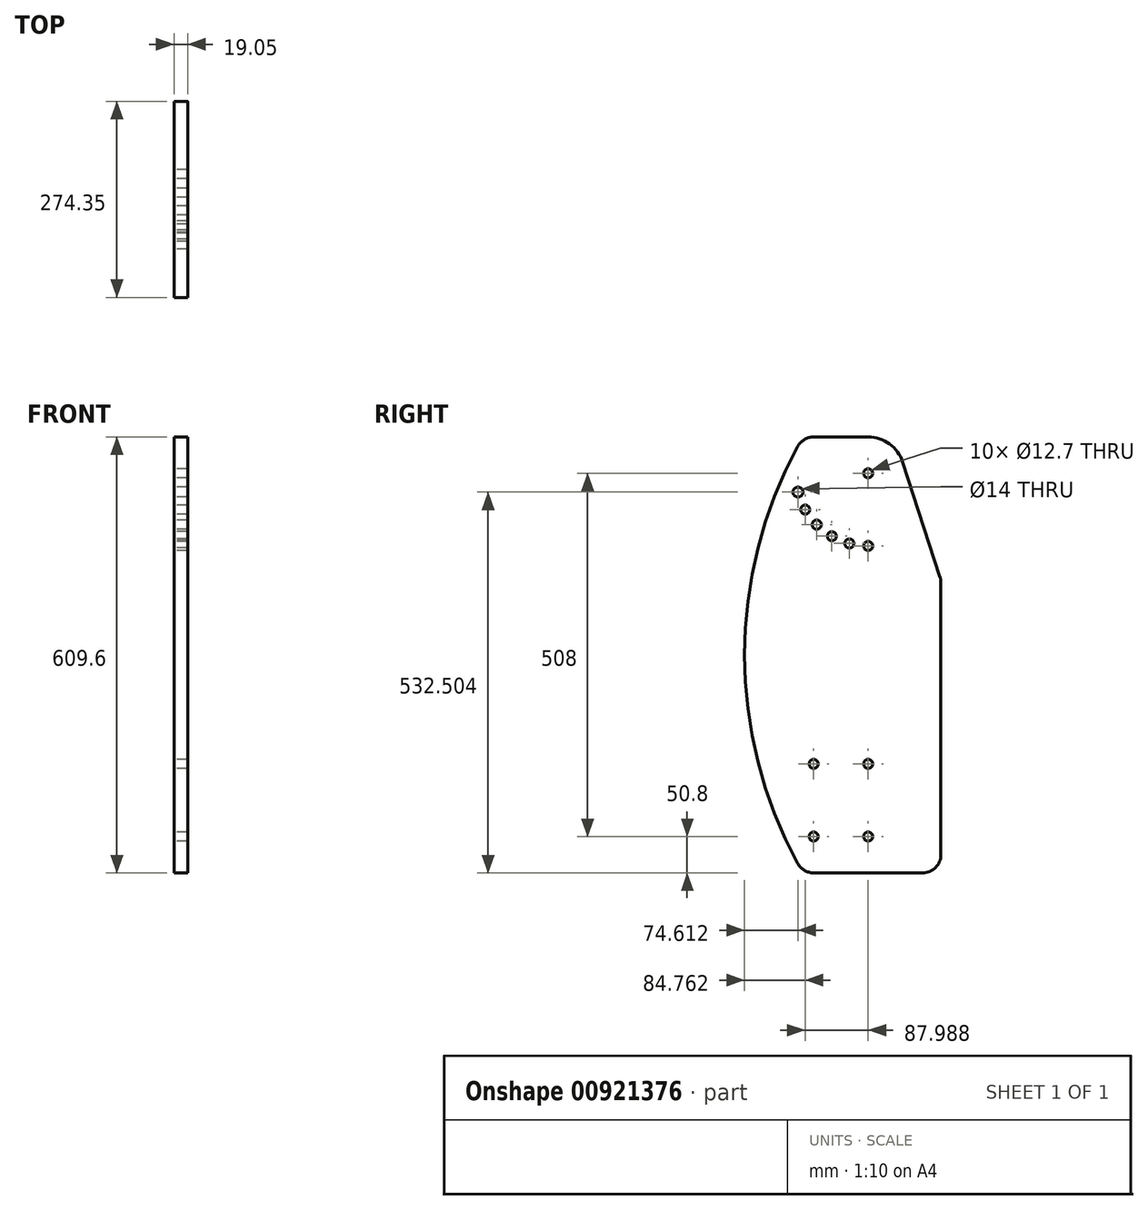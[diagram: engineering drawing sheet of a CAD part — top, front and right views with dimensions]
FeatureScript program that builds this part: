
annotation { "Feature Type Name" : "Feature", "Feature Type Description" : "" }
export const myFeature = defineFeature(function(context is Context, id is Id, definition is map)
    precondition{}
    {
        {
            var Q0;
            Q0=qCreatedBy(makeId("Right.planeOp"),FACE);
            var sketch = newSketch(context, id + "F0", { "sketchPlane" : qUnion([Q0])});
            skLineSegment(sketch, "E0.bottom", {"start": v(-101.6, 304.8) * mm, "end": v(101.6, 304.8) * mm, "construction": true});
            skLineSegment(sketch, "E0.top", {"start": v(-101.6, -304.8) * mm, "end": v(101.6, -304.8) * mm, "construction": true});
            skLineSegment(sketch, "E0.left", {"start": v(-101.6, 304.8) * mm, "end": v(-101.6, -304.8) * mm, "construction": true});
            skLineSegment(sketch, "E0.right", {"start": v(101.6, 304.8) * mm, "end": v(101.6, -304.8) * mm, "construction": true});
            skLineSegment(sketch, "E1", {"start": v(-101.6, 304.8) * mm, "end": v(101.6, -304.8) * mm, "construction": true});
            skLineSegment(sketch, "E2", {"start": v(0, 304.8) * mm, "end": v(0, -304.8) * mm, "construction": true});
            skCircle(sketch, "E3", {"center": v(0, 254) * mm, "radius": 6.35 * mm});
            skArc(sketch, "E4", {"start": v(101.6, 254) * mm, "mid": v(-74.05, 323.56) * mm, "end": v(6.35, 152.6) * mm, "construction": true});
            skCircle(sketch, "E5", {"center": v(0, 152.4) * mm, "radius": 6.35 * mm});
            skLineSegment(sketch, "E6", {"start": v(0, 254) * mm, "end": v(-26.3, 155.86) * mm});
            skLineSegment(sketch, "E7", {"start": v(0, 254) * mm, "end": v(-50.8, 166.01) * mm});
            skLineSegment(sketch, "E8", {"start": v(0, 254) * mm, "end": v(-71.84, 182.16) * mm});
            skLineSegment(sketch, "E9", {"start": v(0, 254) * mm, "end": v(-87.99, 203.2) * mm});
            skCircle(sketch, "E10", {"center": v(-26.3, 155.86) * mm, "radius": 6.35 * mm});
            skCircle(sketch, "E11", {"center": v(-50.8, 166.01) * mm, "radius": 6.35 * mm});
            skCircle(sketch, "E12", {"center": v(-71.84, 182.16) * mm, "radius": 6.35 * mm});
            skCircle(sketch, "E13", {"center": v(-87.99, 203.2) * mm, "radius": 6.35 * mm});
            skLineSegment(sketch, "E14.bottom", {"start": v(-76.2, -152.4) * mm, "end": v(0, -152.4) * mm, "construction": true});
            skLineSegment(sketch, "E14.top", {"start": v(-76.2, -254) * mm, "end": v(0, -254) * mm, "construction": true});
            skLineSegment(sketch, "E14.left", {"start": v(-76.2, -152.4) * mm, "end": v(-76.2, -254) * mm, "construction": true});
            skLineSegment(sketch, "E14.right", {"start": v(0, -152.4) * mm, "end": v(0, -254) * mm, "construction": true});
            skCircle(sketch, "E15", {"center": v(-76.2, -152.4) * mm, "radius": 6.35 * mm});
            skCircle(sketch, "E16", {"center": v(0, -152.4) * mm, "radius": 6.35 * mm});
            skCircle(sketch, "E17", {"center": v(-76.2, -254) * mm, "radius": 6.35 * mm});
            skCircle(sketch, "E18", {"center": v(0, -254) * mm, "radius": 6.35 * mm});
            skArc(sketch, "E19", {"start": v(76.2, -304.8) * mm, "mid": v(94.16, -297.36) * mm, "end": v(101.6, -279.4) * mm});
            skArc(sketch, "E20", {"start": v(-98.5, -291.55) * mm, "mid": v(-89.17, -301.24) * mm, "end": v(-76.2, -304.8) * mm});
            skArc(sketch, "E21", {"start": v(-76.2, 304.8) * mm, "mid": v(-89.17, 301.24) * mm, "end": v(-98.5, 291.55) * mm});
            skArc(sketch, "E22", {"start": v(-98.5, 291.55) * mm, "mid": v(-172.75, 0) * mm, "end": v(-98.5, -291.55) * mm});
            skLineSegment(sketch, "E23", {"start": v(-76.2, 304.8) * mm, "end": v(101.6, 304.8) * mm});
            skLineSegment(sketch, "E24", {"start": v(-76.2, -304.8) * mm, "end": v(76.2, -304.8) * mm});
            skLineSegment(sketch, "E25", {"start": v(101.6, -279.4) * mm, "end": v(101.6, 304.8) * mm});
            skCircle(sketch, "E26", {"center": v(-98.14, 227.7) * mm, "radius": 7 * mm});
            skLineSegment(sketch, "E27", {"start": v(0, 254) * mm, "end": v(-98.14, 227.7) * mm, "construction": true});
            skSolve(sketch);
        }
        {
            var Q0;
            Q0 = qSketchRegion(id + "F0", true);
            extrude(context, id + "F1", {"entities" : qUnion([Q0]), "depth" : 19.05 * mm, "offsetDistance" : 25.4 * mm});
        }
        {
            var Q0;
            Q0=makeQuery(id+"F1.opExtrude","CAP_FACE",FACE,{"disambiguationData":[OSD([sQuery(id+"F0.wireOp",EDGE,"E3"),sQuery(id+"F0.wireOp",EDGE,"E5"),sQuery(id+"F0.wireOp",EDGE,"E10"),sQuery(id+"F0.wireOp",EDGE,"E11"),sQuery(id+"F0.wireOp",EDGE,"E12"),sQuery(id+"F0.wireOp",EDGE,"E13"),sQuery(id+"F0.wireOp",EDGE,"E15"),sQuery(id+"F0.wireOp",EDGE,"E16"),sQuery(id+"F0.wireOp",EDGE,"E17"),sQuery(id+"F0.wireOp",EDGE,"E18"),sQuery(id+"F0.wireOp",EDGE,"E19"),sQuery(id+"F0.wireOp",EDGE,"E20"),sQuery(id+"F0.wireOp",EDGE,"E21"),sQuery(id+"F0.wireOp",EDGE,"E22"),sQuery(id+"F0.wireOp",EDGE,"E23"),sQuery(id+"F0.wireOp",EDGE,"E24"),sQuery(id+"F0.wireOp",EDGE,"E25"),sQuery(id+"F0.wireOp",EDGE,"E26")])],"isStart":true});
            var sketch = newSketch(context, id + "F2", { "sketchPlane" : qUnion([Q0])});
            skArc(sketch, "E28", {"start": v(0, 304.8) * mm, "mid": v(-29.86, 295.1) * mm, "end": v(-48.32, 269.7) * mm});
            skLineSegment(sketch, "E29", {"start": v(-100.36, 109.45) * mm, "end": v(-48.32, 269.7) * mm});
            skLineSegment(sketch, "E30", {"start": v(-101.6, 101.6) * mm, "end": v(-101.6, 304.8) * mm});
            skLineSegment(sketch, "E31", {"start": v(-101.6, 304.8) * mm, "end": v(0, 304.8) * mm});
            skLineSegment(sketch, "E32", {"start": v(-101.6, 101.6) * mm, "end": v(0, 101.6) * mm, "construction": true});
            skArc(sketch, "E33", {"start": v(-100.36, 109.45) * mm, "mid": v(-101.29, 105.57) * mm, "end": v(-101.6, 101.6) * mm});
            skSolve(sketch);
        }
        {
            var Q0;
            Q0 = qSketchRegion(id + "F2", true);
            extrude(context, id + "F3", {"entities" : qUnion([Q0]), "operationType" : NewBodyOperationType.REMOVE, "endBound" : BoundingType.THROUGH_ALL, "oppositeDirection" : true, "depth" : 25.4 * mm, "offsetDistance" : 25.4 * mm});
        }
    });
